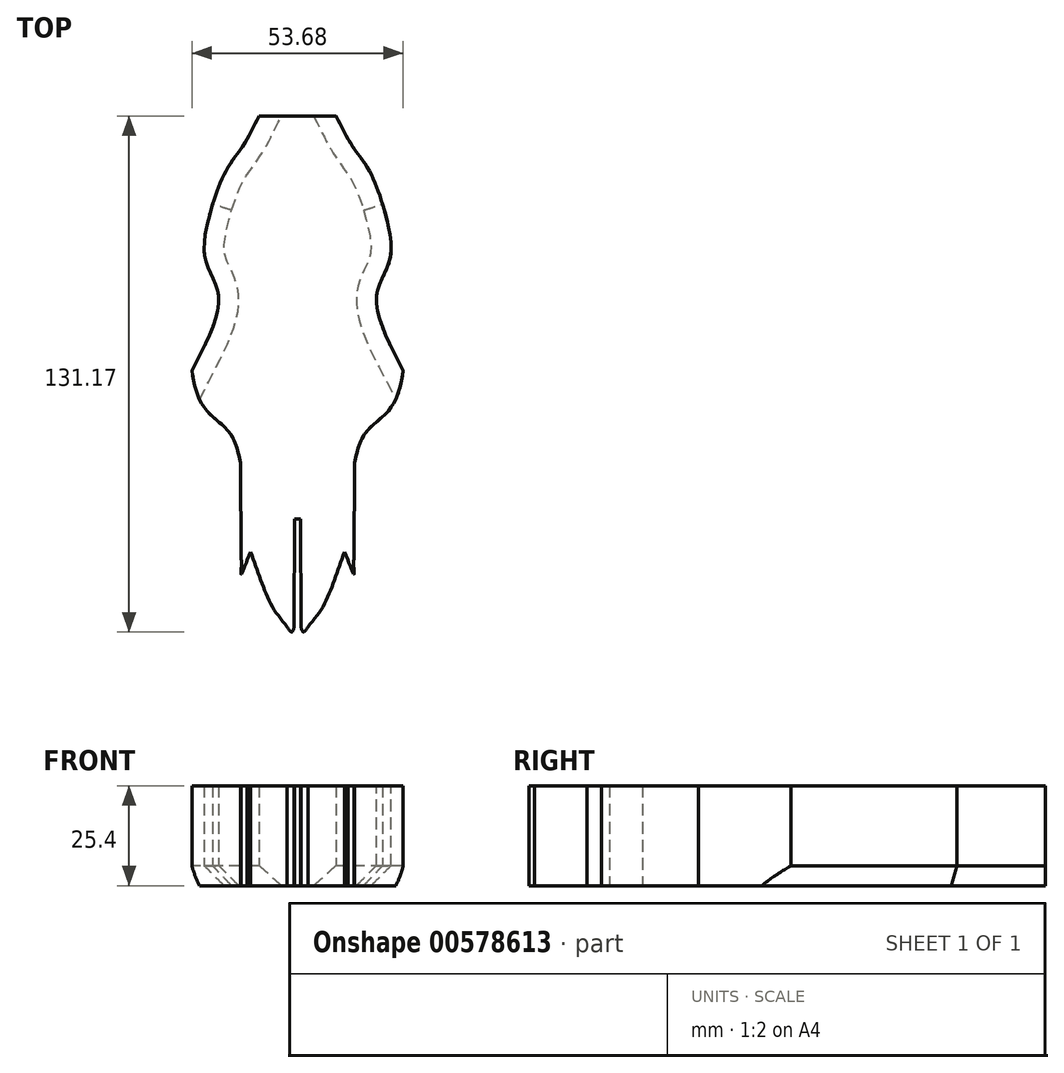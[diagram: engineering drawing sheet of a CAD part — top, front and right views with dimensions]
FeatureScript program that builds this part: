
annotation { "Feature Type Name" : "Feature", "Feature Type Description" : "" }
export const myFeature = defineFeature(function(context is Context, id is Id, definition is map)
    precondition{}
    {
        {
            var Q0;
            Q0=qCreatedBy(makeId("Top.planeOp"),FACE);
            var sketch = newSketch(context, id + "F0", { "sketchPlane" : qUnion([Q0])});
            skFitSpline(sketch, "E0", {"points": [v(-14.3, -68.33) * mm, v(-14.23, -69.6) * mm, v(-14.35, -72) * mm, v(-12.79, -68.41) * mm]});
            skLineSegment(sketch, "E1", {"start": v(-14.5, -43.8) * mm, "end": v(-14.3, -68.33) * mm});
            skFitSpline(sketch, "E2", {"points": [v(-11.9, -66.35) * mm, v(-9.42, -73.26) * mm, v(-6.64, -79.9) * mm, v(-2.64, -85.4) * mm]});
            skFitSpline(sketch, "E3", {"points": [v(-2.64, -85.4) * mm, v(-1.5, -86.75) * mm, v(-1.11, -86.24) * mm, v(-0.85, -85.44) * mm]});
            skLineSegment(sketch, "E4", {"start": v(-12.79, -68.41) * mm, "end": v(-11.9, -66.35) * mm});
            skLineSegment(sketch, "E5", {"start": v(-0.85, -85.44) * mm, "end": v(-0.8, -58.01) * mm});
            skLineSegment(sketch, "E6", {"start": v(-0.8, -58.01) * mm, "end": v(0.07, -58.01) * mm});
            skPoint(sketch, "E7", {"position": v(0, 0) * mm});
            skLineSegment(sketch, "E8.MirrorCS", {"start": v(12.79, -68.41) * mm, "end": v(11.9, -66.35) * mm});
            skFitSpline(sketch, "E9.MirrorCS", {"points": [v(2.64, -85.4) * mm, v(1.5, -86.75) * mm, v(1.11, -86.24) * mm, v(0.85, -85.44) * mm]});
            skFitSpline(sketch, "E10.MirrorCS", {"points": [v(14.3, -68.33) * mm, v(14.23, -69.6) * mm, v(14.35, -72) * mm, v(12.79, -68.41) * mm]});
            skLineSegment(sketch, "E11.MirrorCS", {"start": v(0.8, -58.01) * mm, "end": v(-0.07, -58.01) * mm});
            skLineSegment(sketch, "E12.MirrorCS", {"start": v(0.85, -85.44) * mm, "end": v(0.8, -58.01) * mm});
            skFitSpline(sketch, "E13.MirrorCS", {"points": [v(11.9, -66.35) * mm, v(9.42, -73.26) * mm, v(6.64, -79.9) * mm, v(2.64, -85.4) * mm]});
            skLineSegment(sketch, "E14.MirrorCS", {"start": v(14.5, -43.8) * mm, "end": v(14.3, -68.33) * mm});
            skFitSpline(sketch, "E15.MirrorCS", {"points": [v(26.84, -20.27) * mm, v(23.82, -29.57) * mm, v(17.24, -36.16) * mm, v(14.5, -43.8) * mm]});
            skFitSpline(sketch, "E16.MirrorCS", {"points": [v(21.63, 21.95) * mm, v(23.47, 8.06) * mm, v(20.05, -1.5) * mm, v(26.84, -20.27) * mm]});
            skFitSpline(sketch, "E17.MirrorCS", {"points": [v(9.77, 44.42) * mm, v(13.77, 37) * mm, v(18.28, 30.34) * mm, v(21.63, 21.95) * mm]});
            skLineSegment(sketch, "E18", {"start": v(-9.77, 44.42) * mm, "end": v(9.77, 44.42) * mm});
            skFitSpline(sketch, "E19.MirrorCS", {"points": [v(-26.84, -20.27) * mm, v(-23.82, -29.57) * mm, v(-17.24, -36.16) * mm, v(-14.5, -43.8) * mm]});
            skFitSpline(sketch, "E20.MirrorCS", {"points": [v(-9.77, 44.42) * mm, v(-13.77, 37) * mm, v(-18.28, 30.34) * mm, v(-21.63, 21.95) * mm]});
            skFitSpline(sketch, "E21.MirrorCS", {"points": [v(-21.63, 21.95) * mm, v(-23.47, 8.06) * mm, v(-20.05, -1.5) * mm, v(-26.84, -20.27) * mm]});
            skSolve(sketch);
        }
        {
            var Q0;
            Q0 = qSketchRegion(id + "F0", true);
            extrude(context, id + "F1", {"entities" : qUnion([Q0]), "depth" : 25.4 * mm, "offsetDistance" : 25.4 * mm});
        }
        {
            var Q0;
            Q0=makeQuery(id+"F1.opExtrude","CAP_EDGE",EDGE,{"disambiguationData":[OSD([sQuery(id+"F0.wireOp",EDGE,"482aa96b-e135-4952-bb85-f0bd7762c0fd")])],"isStart":true});
            var Q1;
            Q1=makeQuery(id+"F1.opExtrude","CAP_EDGE",EDGE,{"disambiguationData":[OSD([sQuery(id+"F0.wireOp",EDGE,"E17.MirrorCS")])],"isStart":true});
            var Q2;
            Q2=makeQuery(id+"F1.opExtrude","CAP_EDGE",EDGE,{"disambiguationData":[OSD([sQuery(id+"F0.wireOp",EDGE,"1bb5bfc9-032c-4283-987e-81e23f5d6941")])],"isStart":true});
            var Q3;
            Q3=makeQuery(id+"F1.opExtrude","CAP_EDGE",EDGE,{"disambiguationData":[OSD([sQuery(id+"F0.wireOp",EDGE,"E16.MirrorCS")])],"isStart":true});
            var Q4;
            Q4=makeQuery(id+"F1.opExtrude","CAP_EDGE",EDGE,{"disambiguationData":[OSD([sQuery(id+"F0.wireOp",EDGE,"E20.MirrorCS")])],"isStart":true});
            var Q5;
            Q5=makeQuery(id+"F1.opExtrude","CAP_EDGE",EDGE,{"disambiguationData":[OSD([sQuery(id+"F0.wireOp",EDGE,"E21.MirrorCS")])],"isStart":true});
            chamfer(context, id + "F2", {"entities" : qUnion([Q0, Q1, Q2, Q3, Q4, Q5]), "width" : 5.08 * mm, "tangentPropagation" : true});
        }
    });
